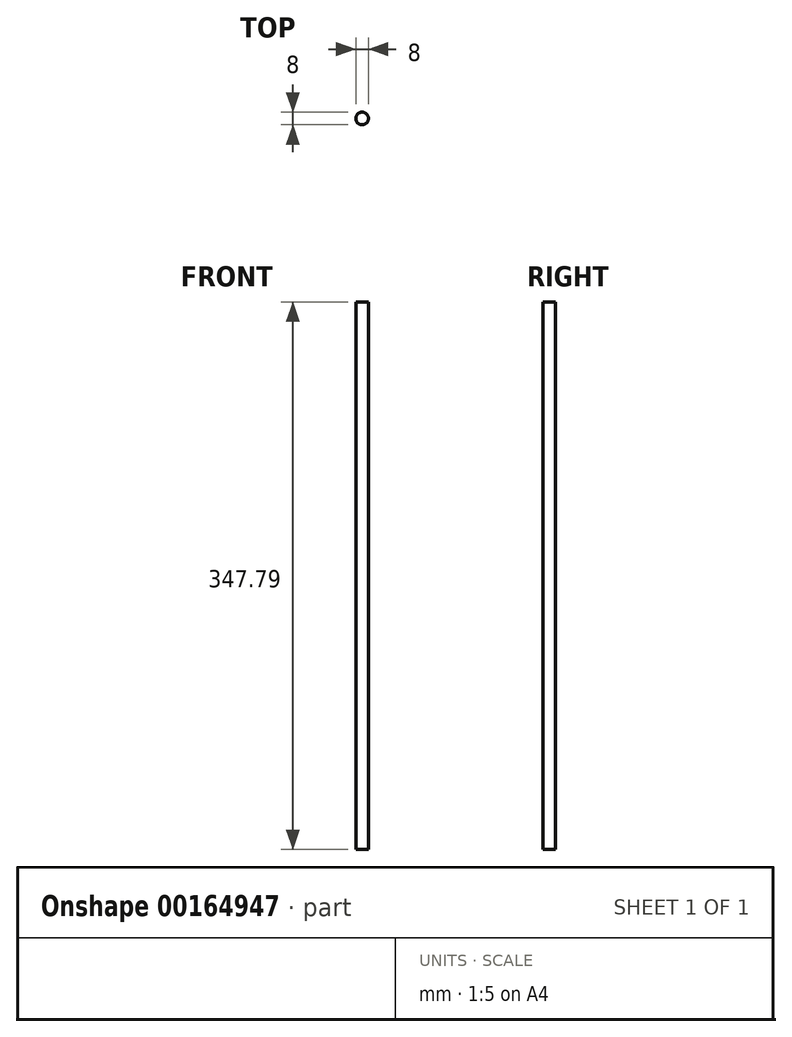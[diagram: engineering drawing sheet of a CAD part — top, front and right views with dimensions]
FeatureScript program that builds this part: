
annotation { "Feature Type Name" : "Feature", "Feature Type Description" : "" }
export const myFeature = defineFeature(function(context is Context, id is Id, definition is map)
    precondition{}
    {
        {
            var Q0;
            Q0=qCreatedBy(makeId("Top.planeOp"),FACE);
            var sketch = newSketch(context, id + "F0", { "sketchPlane" : qUnion([Q0])});
            skCircle(sketch, "E0", {"center": v(0, 0) * mm, "radius": 4 * mm});
            skSolve(sketch);
        }
        {
            var Q0;
            Q0 = qSketchRegion(id + "F0", true);
            extrude(context, id + "F1", {"entities" : qUnion([Q0]), "depth" : 347.8 * mm});
        }
    });
